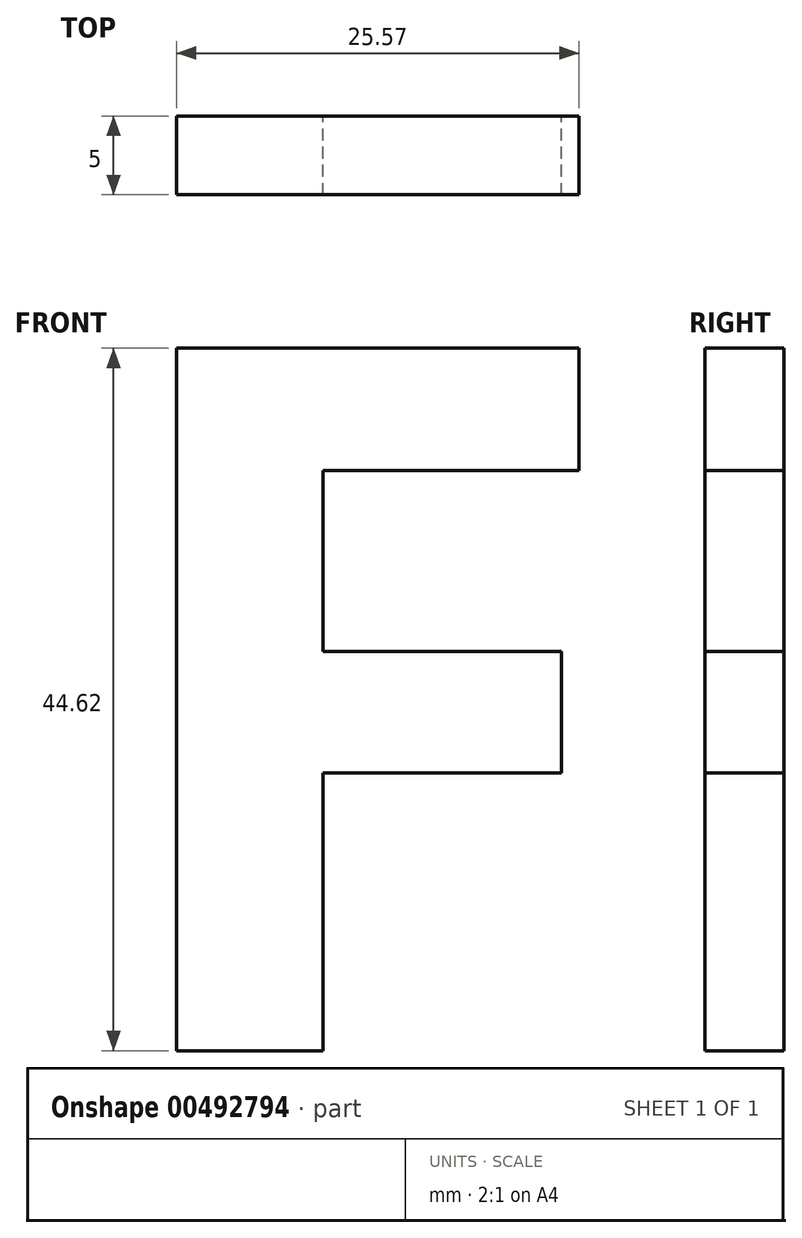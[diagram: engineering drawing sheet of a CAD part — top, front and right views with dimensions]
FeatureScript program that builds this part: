
annotation { "Feature Type Name" : "Feature", "Feature Type Description" : "" }
export const myFeature = defineFeature(function(context is Context, id is Id, definition is map)
    precondition{}
    {
        {
            var Q0;
            Q0=qCreatedBy(makeId("Front.planeOp"),FACE);
            var sketch = newSketch(context, id + "F0", { "sketchPlane" : qUnion([Q0])});
            skText(sketch, "E0", { "text": "F", "fontName": "OpenSans-Bold.ttf"});
            const initialGuessF0  = {"E0": [-0.07145, 0.01579, 1, 0, 0.045]};
            skSetInitialGuess(sketch, initialGuessF0);
            skSolve(sketch);
        }
        {
            var Q0;
            Q0=makeQuery(id+"F0.imprint","IMPRINT",FACE,{"disambiguationData":[TD([[makeQuery(id+"F0.imprint","IMPRINT",EDGE,{"derivedFrom":sQuery(id+"F0.wireOp",EDGE,"E0.sketch_text.stroke-0")}),-1.0]])]});
            extrude(context, id + "F1", {"entities" : qUnion([Q0]), "depth" : 5 * mm});
        }
    });
